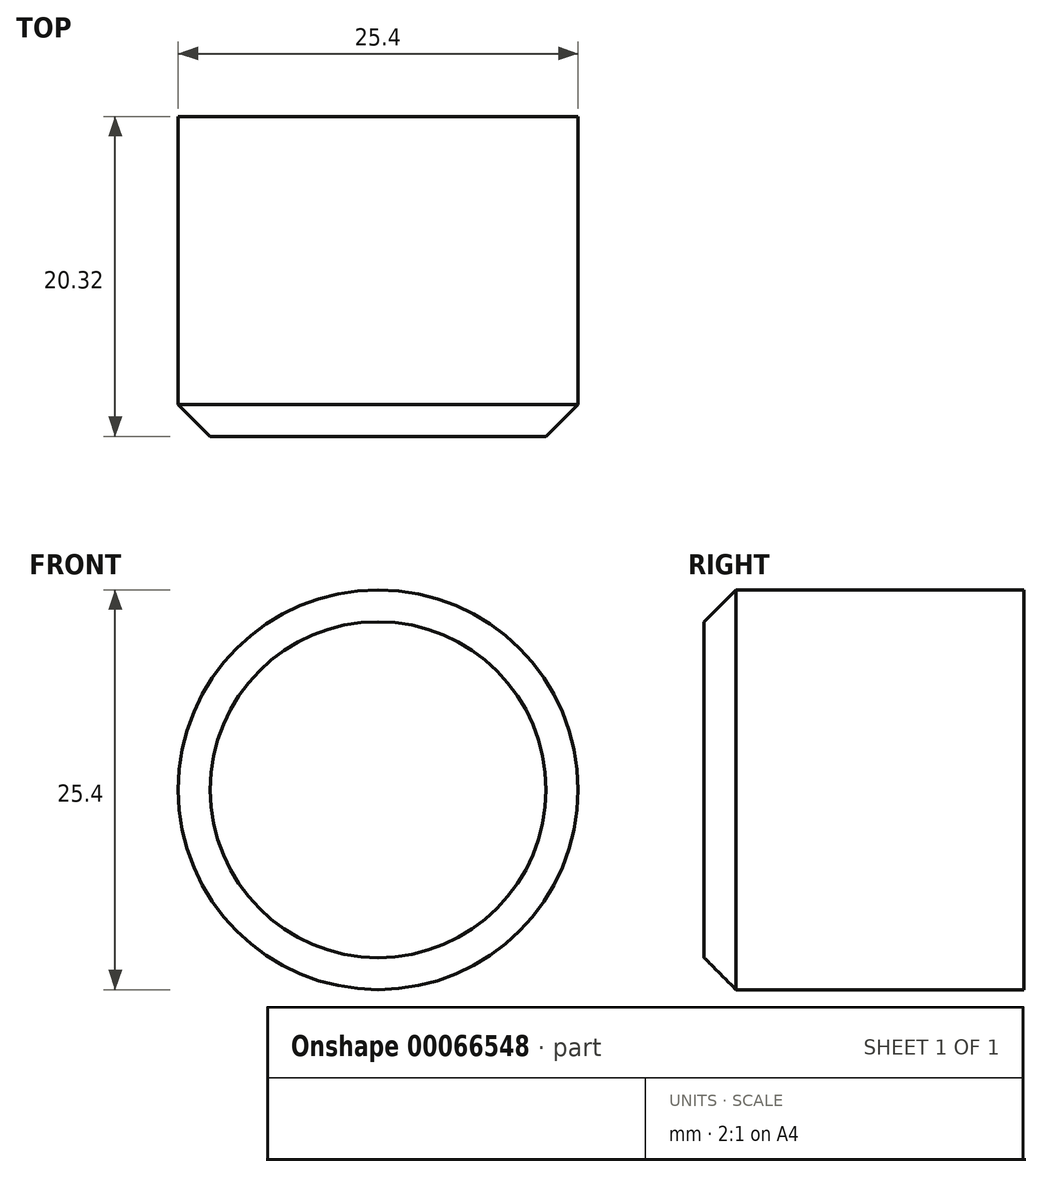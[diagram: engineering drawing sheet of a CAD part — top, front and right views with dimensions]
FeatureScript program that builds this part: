
annotation { "Feature Type Name" : "Feature", "Feature Type Description" : "" }
export const myFeature = defineFeature(function(context is Context, id is Id, definition is map)
    precondition{}
    {
        {
            var Q0;
            Q0=qCreatedBy(makeId("Front.planeOp"),FACE);
            var sketch = newSketch(context, id + "F0", { "sketchPlane" : qUnion([Q0])});
            skCircle(sketch, "E0", {"center": v(17.97, 22.36) * mm, "radius": 12.7 * mm});
            skSolve(sketch);
        }
        {
            var Q0;
            Q0=makeQuery(id+"F0.imprint","IMPRINT",FACE,{"disambiguationData":[TD([[makeQuery(id+"F0.imprint","IMPRINT",EDGE,{"derivedFrom":sQuery(id+"F0.wireOp",EDGE,"E0")}),1.0]])]});
            extrude(context, id + "F1", {"entities" : qUnion([Q0]), "depth" : 20.32 * mm});
        }
        {
            var Q0;
            Q0=makeQuery(id+"F1.opExtrude","CAP_EDGE",EDGE,{"disambiguationData":[OSD([sQuery(id+"F0.wireOp",EDGE,"E0")])],"isStart":false});
            chamfer(context, id + "F2", {"entities" : qUnion([Q0]), "width" : 2.03 * mm, "tangentPropagation" : true});
        }
    });
